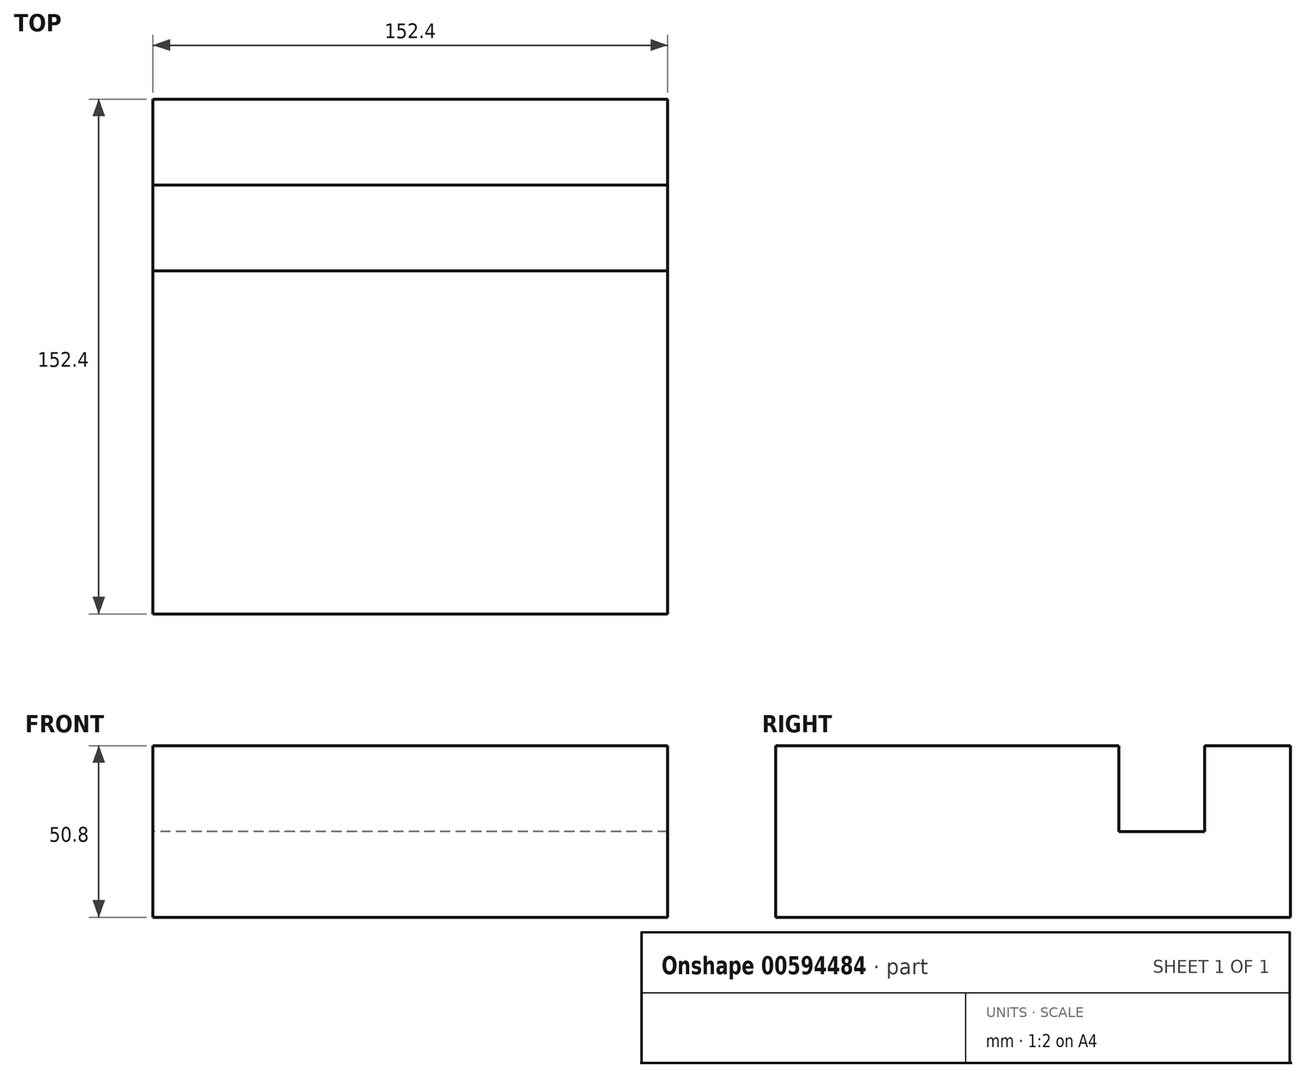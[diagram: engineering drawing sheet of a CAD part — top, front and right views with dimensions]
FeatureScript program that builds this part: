
annotation { "Feature Type Name" : "Feature", "Feature Type Description" : "" }
export const myFeature = defineFeature(function(context is Context, id is Id, definition is map)
    precondition{}
    {
        {
            var Q0;
            Q0=qCreatedBy(makeId("Right.planeOp"),FACE);
            var sketch = newSketch(context, id + "F0", { "sketchPlane" : qUnion([Q0])});
            skLineSegment(sketch, "E0", {"start": v(0, 0) * mm, "end": v(152.4, 0) * mm});
            skLineSegment(sketch, "E1", {"start": v(152.4, 0) * mm, "end": v(152.4, 50.8) * mm});
            skLineSegment(sketch, "E2", {"start": v(152.4, 50.8) * mm, "end": v(127, 50.8) * mm});
            skLineSegment(sketch, "E3", {"start": v(127, 50.8) * mm, "end": v(127, 25.4) * mm});
            skLineSegment(sketch, "E4", {"start": v(127, 25.4) * mm, "end": v(101.6, 25.4) * mm});
            skLineSegment(sketch, "E5", {"start": v(101.6, 25.4) * mm, "end": v(101.6, 50.8) * mm});
            skLineSegment(sketch, "E6", {"start": v(101.6, 50.8) * mm, "end": v(0, 50.8) * mm});
            skLineSegment(sketch, "E7", {"start": v(0, 50.8) * mm, "end": v(0, 0) * mm});
            skSolve(sketch);
        }
        {
            var Q0;
            Q0=makeQuery(id+"F0.imprint","IMPRINT",FACE,{"disambiguationData":[TD([[makeQuery(id+"F0.imprint","IMPRINT",EDGE,{"derivedFrom":sQuery(id+"F0.wireOp",EDGE,"E0")}),1.0]])]});
            extrude(context, id + "F1", {"entities" : qUnion([Q0]), "depth" : 152.4 * mm, "offsetDistance" : 25.4 * mm});
        }
    });
